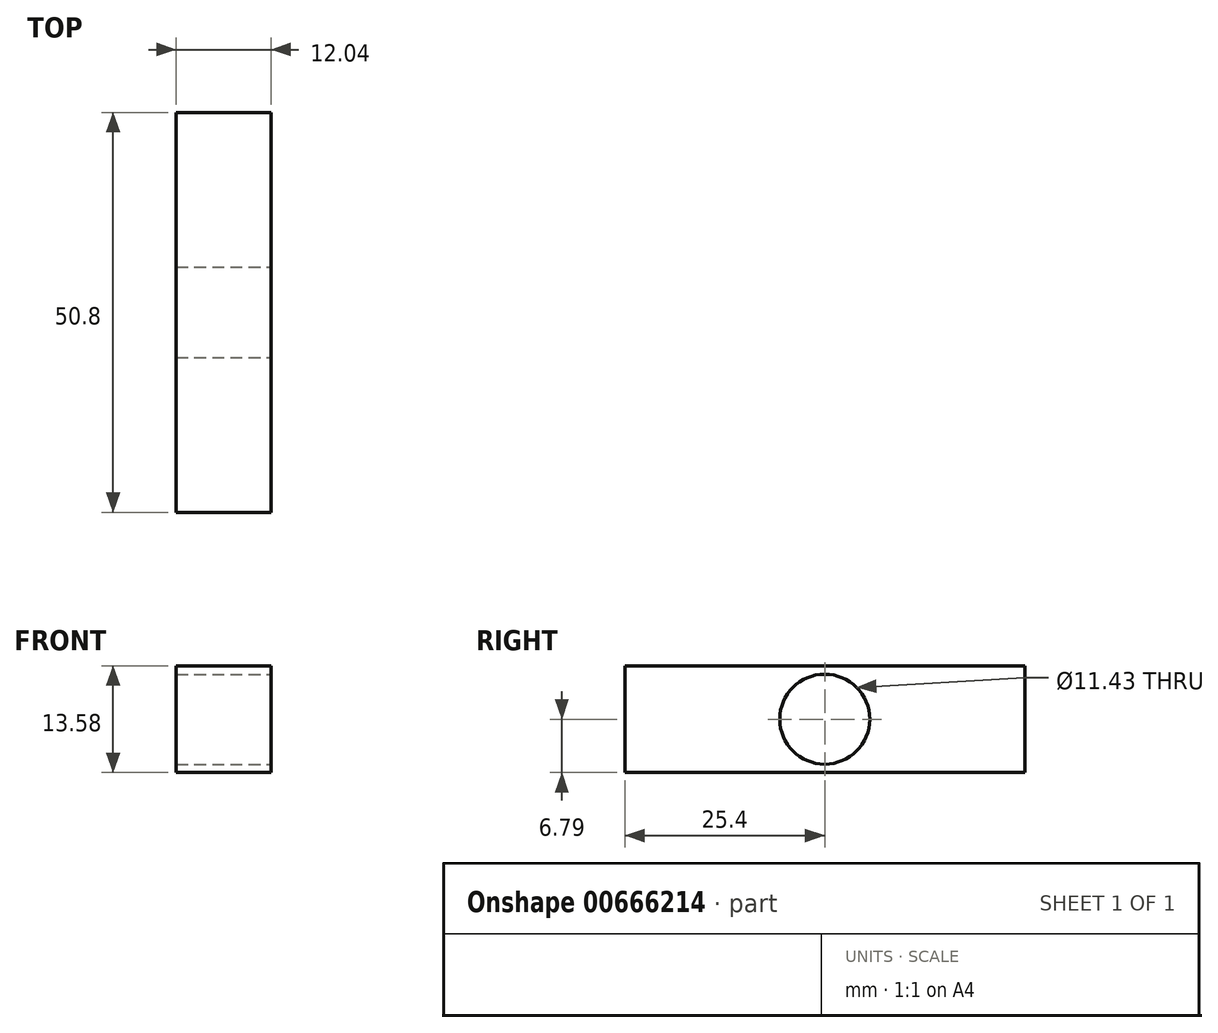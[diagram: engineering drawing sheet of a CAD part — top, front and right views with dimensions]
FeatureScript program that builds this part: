
annotation { "Feature Type Name" : "Feature", "Feature Type Description" : "" }
export const myFeature = defineFeature(function(context is Context, id is Id, definition is map)
    precondition{}
    {
        {
            var Q0;
            Q0=qCreatedBy(makeId("Front.planeOp"),FACE);
            var sketch = newSketch(context, id + "F0", { "sketchPlane" : qUnion([Q0])});
            skLineSegment(sketch, "E0.bottom", {"start": v(6.02, -6.8) * mm, "end": v(-6.02, -6.8) * mm});
            skLineSegment(sketch, "E0.top", {"start": v(6.02, 6.8) * mm, "end": v(-6.02, 6.8) * mm});
            skLineSegment(sketch, "E0.left", {"start": v(6.02, -6.8) * mm, "end": v(6.02, 6.8) * mm});
            skLineSegment(sketch, "E0.right", {"start": v(-6.02, -6.8) * mm, "end": v(-6.02, 6.8) * mm});
            skPoint(sketch, "E0.middle", {"position": v(0, 0) * mm});
            skSolve(sketch);
        }
        {
            var Q0;
            Q0=makeQuery(id+"F0.imprint","IMPRINT",FACE,{"disambiguationData":[TD([[makeQuery(id+"F0.imprint","IMPRINT",EDGE,{"derivedFrom":sQuery(id+"F0.wireOp",EDGE,"E0.bottom")}),-1.0]])]});
            extrude(context, id + "F1", {"entities" : qUnion([Q0]), "depth" : 25.4 * mm, "offsetDistance" : 25.4 * mm, "hasSecondDirection" : true, "secondDirectionOppositeDirection" : true, "secondDirectionDepth" : 25.4 * mm});
        }
        {
            var Q0;
            Q0=makeQuery(id+"F1.opExtrude","SWEPT_FACE",FACE,{"disambiguationData":[OSD([sQuery(id+"F0.wireOp",EDGE,"E0.left")])]});
            var sketch = newSketch(context, id + "F2", { "sketchPlane" : qUnion([Q0])});
            skCircle(sketch, "E1", {"center": v(0, 0) * mm, "radius": 5.72 * mm});
            skSolve(sketch);
        }
        {
            var Q0;
            Q0=makeQuery(id+"F2.imprint","IMPRINT",FACE,{"disambiguationData":[TD([[makeQuery(id+"F2.imprint","IMPRINT",EDGE,{"derivedFrom":sQuery(id+"F2.wireOp",EDGE,"E1")}),1.0]])]});
            extrude(context, id + "F3", {"entities" : qUnion([Q0]), "operationType" : NewBodyOperationType.REMOVE, "oppositeDirection" : true, "depth" : 25.4 * mm, "offsetDistance" : 25.4 * mm});
        }
    });
